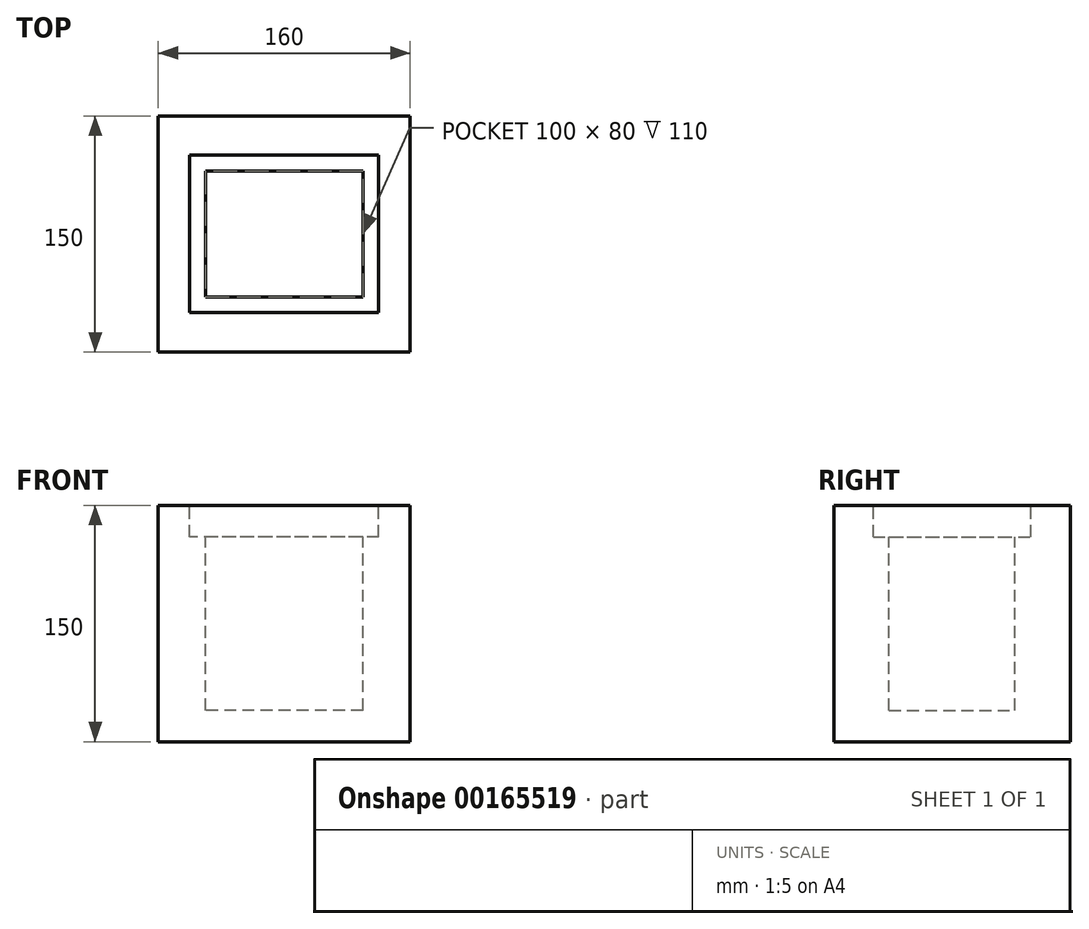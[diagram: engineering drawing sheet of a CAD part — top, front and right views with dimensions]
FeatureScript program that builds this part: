
annotation { "Feature Type Name" : "Feature", "Feature Type Description" : "" }
export const myFeature = defineFeature(function(context is Context, id is Id, definition is map)
    precondition{}
    {
        {
            var Q0;
            Q0=qCreatedBy(makeId("Front.planeOp"),FACE);
            var sketch = newSketch(context, id + "F0", { "sketchPlane" : qUnion([Q0])});
            skLineSegment(sketch, "E0.bottom", {"start": v(80, -75) * mm, "end": v(-80, -75) * mm});
            skLineSegment(sketch, "E0.top", {"start": v(80, 75) * mm, "end": v(-80, 75) * mm});
            skLineSegment(sketch, "E0.left", {"start": v(80, -75) * mm, "end": v(80, 75) * mm});
            skLineSegment(sketch, "E0.right", {"start": v(-80, -75) * mm, "end": v(-80, 75) * mm});
            skPoint(sketch, "E0.middle", {"position": v(0, 0) * mm});
            skSolve(sketch);
        }
        {
            var Q0;
            Q0 = qSketchRegion(id + "F0", true);
            extrude(context, id + "F1", {"entities" : qUnion([Q0]), "depth" : 150 * mm});
        }
        {
            var Q0;
            Q0=makeQuery(id+"F1.opExtrude","SWEPT_FACE",FACE,{"disambiguationData":[OSD([sQuery(id+"F0.wireOp",EDGE,"E0.top")])]});
            var sketch = newSketch(context, id + "F2", { "sketchPlane" : qUnion([Q0])});
            skLineSegment(sketch, "E1.bottom", {"start": v(60, -125) * mm, "end": v(-60, -125) * mm});
            skLineSegment(sketch, "E1.top", {"start": v(60, -25) * mm, "end": v(-60, -25) * mm});
            skLineSegment(sketch, "E1.left", {"start": v(60, -125) * mm, "end": v(60, -25) * mm});
            skLineSegment(sketch, "E1.right", {"start": v(-60, -125) * mm, "end": v(-60, -25) * mm});
            skPoint(sketch, "E1.middle", {"position": v(0, -75) * mm});
            skPoint(sketch, "E1.middle.positionSnap0", {"position": v(-80, -75) * mm});
            skPoint(sketch, "E1.centerSnap0", {"position": v(-80, -75) * mm});
            skSolve(sketch);
        }
        {
            var Q0;
            Q0 = qSketchRegion(id + "F2", true);
            extrude(context, id + "F3", {"entities" : qUnion([Q0]), "operationType" : NewBodyOperationType.REMOVE, "oppositeDirection" : true, "depth" : 20 * mm});
        }
        {
            var Q0;
            Q0=makeQuery(id+"F3.boolean.opBoolean","COPY",FACE,{"derivedFrom":makeQuery(id+"F3.opExtrude","CAP_FACE",FACE,{"disambiguationData":[OSD([sQuery(id+"F2.wireOp",EDGE,"E1.bottom"),sQuery(id+"F2.wireOp",EDGE,"E1.top"),sQuery(id+"F2.wireOp",EDGE,"E1.left"),sQuery(id+"F2.wireOp",EDGE,"E1.right")])],"isStart":false})});
            var sketch = newSketch(context, id + "F4", { "sketchPlane" : qUnion([Q0])});
            skLineSegment(sketch, "E2.bottom", {"start": v(50, -115) * mm, "end": v(-50, -115) * mm});
            skLineSegment(sketch, "E2.top", {"start": v(50, -35) * mm, "end": v(-50, -35) * mm});
            skLineSegment(sketch, "E2.left", {"start": v(50, -115) * mm, "end": v(50, -35) * mm});
            skLineSegment(sketch, "E2.right", {"start": v(-50, -115) * mm, "end": v(-50, -35) * mm});
            skPoint(sketch, "E2.middle", {"position": v(0, -75) * mm});
            skPoint(sketch, "E2.middle.positionSnap0", {"position": v(-60, -75) * mm});
            skPoint(sketch, "E2.centerSnap0", {"position": v(-60, -75) * mm});
            skSolve(sketch);
        }
        {
            var Q0;
            Q0 = qSketchRegion(id + "F4", true);
            extrude(context, id + "F5", {"entities" : qUnion([Q0]), "operationType" : NewBodyOperationType.REMOVE, "oppositeDirection" : true, "depth" : 110 * mm});
        }
    });
